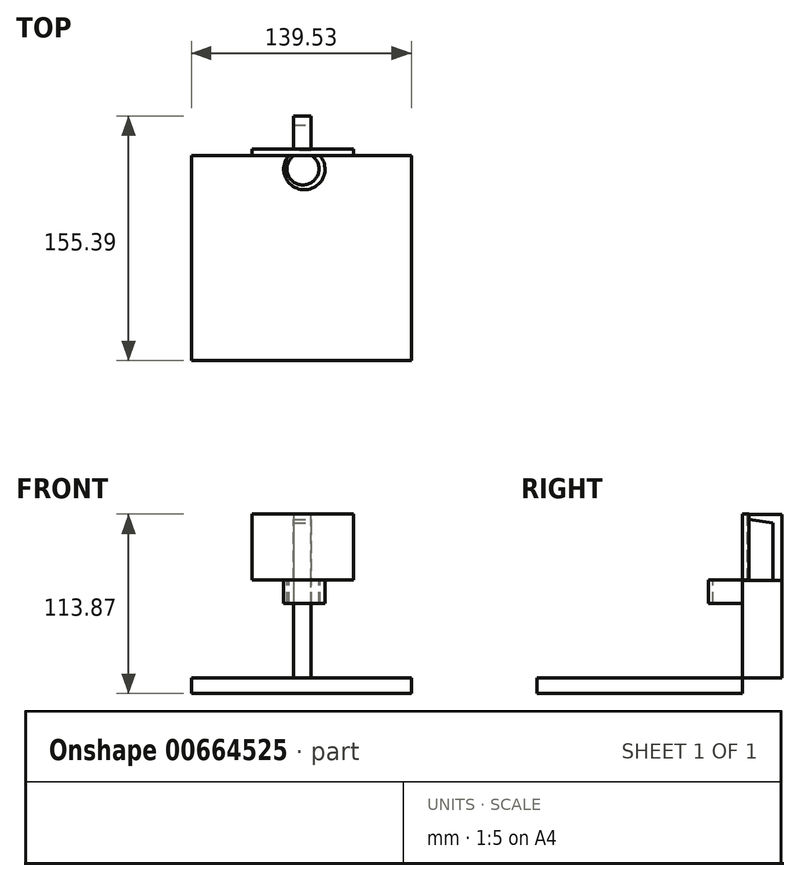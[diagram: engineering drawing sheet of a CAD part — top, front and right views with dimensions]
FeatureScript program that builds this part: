
annotation { "Feature Type Name" : "Feature", "Feature Type Description" : "" }
export const myFeature = defineFeature(function(context is Context, id is Id, definition is map)
    precondition{}
    {
        {
            var Q0;
            Q0=qCreatedBy(makeId("Top.planeOp"),FACE);
            var sketch = newSketch(context, id + "F0", { "sketchPlane" : qUnion([Q0])});
            skLineSegment(sketch, "E0", {"start": v(-70.05, 65.48) * mm, "end": v(-70.05, -64.91) * mm});
            skLineSegment(sketch, "E1", {"start": v(-70.05, -64.91) * mm, "end": v(69.48, -64.91) * mm});
            skLineSegment(sketch, "E2", {"start": v(69.48, -64.91) * mm, "end": v(69.48, 65.48) * mm});
            skLineSegment(sketch, "E3", {"start": v(69.48, 65.48) * mm, "end": v(-70.05, 65.48) * mm});
            skSolve(sketch);
        }
        {
            var Q0;
            Q0=makeQuery(id+"F0.imprint","IMPRINT",FACE,{"disambiguationData":[TD([[makeQuery(id+"F0.imprint","IMPRINT",EDGE,{"derivedFrom":sQuery(id+"F0.wireOp",EDGE,"E0")}),1.0]])]});
            extrude(context, id + "F1", {"entities" : qUnion([Q0]), "oppositeDirection" : true, "depth" : 10 * mm, "offsetDistance" : 25 * mm});
        }
        {
            var Q0;
            Q0=makeQuery(id+"F1.opExtrude","SWEPT_FACE",FACE,{"disambiguationData":[OSD([sQuery(id+"F0.wireOp",EDGE,"E3")])]});
            var sketch = newSketch(context, id + "F2", { "sketchPlane" : qUnion([Q0])});
            skLineSegment(sketch, "E4", {"start": v(-6.13, 0) * mm, "end": v(-6.13, 62.06) * mm});
            skLineSegment(sketch, "E5", {"start": v(-6.13, 62.06) * mm, "end": v(5.28, 62.06) * mm});
            skLineSegment(sketch, "E6", {"start": v(5.28, 62.06) * mm, "end": v(5.28, 0) * mm});
            skLineSegment(sketch, "E7", {"start": v(5.28, 0) * mm, "end": v(-6.13, 0) * mm});
            skLineSegment(sketch, "E8", {"start": v(-6.13, 62.06) * mm, "end": v(-32.65, 62.06) * mm});
            skLineSegment(sketch, "E9", {"start": v(-32.65, 62.06) * mm, "end": v(-32.65, 103.87) * mm});
            skLineSegment(sketch, "E10", {"start": v(-32.65, 103.87) * mm, "end": v(31.8, 103.87) * mm});
            skLineSegment(sketch, "E11", {"start": v(31.8, 103.87) * mm, "end": v(31.8, 62.06) * mm});
            skLineSegment(sketch, "E12", {"start": v(31.8, 62.06) * mm, "end": v(5.28, 62.06) * mm});
            skSolve(sketch);
        }
        {
            var Q0;
            Q0=makeQuery(id+"F2.imprint","IMPRINT",FACE,{"disambiguationData":[TD([[makeQuery(id+"F2.imprint","IMPRINT",EDGE,{"derivedFrom":sQuery(id+"F2.wireOp",EDGE,"E5")}),1.0]])]});
            extrude(context, id + "F3", {"entities" : qUnion([Q0]), "depth" : 4 * mm, "offsetDistance" : 25 * mm});
        }
        {
            var Q0;
            Q0=makeQuery(id+"F1.opExtrude","SWEPT_FACE",FACE,{"disambiguationData":[OSD([sQuery(id+"F0.wireOp",EDGE,"E3")])]});
            var sketch = newSketch(context, id + "F4", { "sketchPlane" : qUnion([Q0])});
            skLineSegment(sketch, "E13", {"start": v(5.27, 61.9) * mm, "end": v(5.27, 0) * mm});
            skLineSegment(sketch, "E14", {"start": v(5.27, 0) * mm, "end": v(-5.95, 0) * mm});
            skLineSegment(sketch, "E15", {"start": v(-5.95, 0) * mm, "end": v(-5.95, 61.9) * mm});
            skLineSegment(sketch, "E16", {"start": v(-5.95, 61.9) * mm, "end": v(5.27, 61.9) * mm});
            skSolve(sketch);
        }
        {
            var Q0;
            Q0=makeQuery(id+"F4.imprint","IMPRINT",FACE,{"disambiguationData":[TD([[makeQuery(id+"F4.imprint","IMPRINT",EDGE,{"derivedFrom":sQuery(id+"F4.wireOp",EDGE,"E13")}),-1.0]])]});
            extrude(context, id + "F5", {"entities" : qUnion([Q0]), "depth" : 25 * mm, "offsetDistance" : 25 * mm});
        }
        {
            var Q0;
            Q0=makeQuery(id+"F5.opExtrude","CAP_FACE",FACE,{"disambiguationData":[OSD([sQuery(id+"F4.wireOp",EDGE,"E13"),sQuery(id+"F4.wireOp",EDGE,"E14"),sQuery(id+"F4.wireOp",EDGE,"E15"),sQuery(id+"F4.wireOp",EDGE,"E16")])],"isStart":false});
            var sketch = newSketch(context, id + "F6", { "sketchPlane" : qUnion([Q0])});
            skLineSegment(sketch, "E17", {"start": v(-5.95, 61.9) * mm, "end": v(-5.95, 103.76) * mm});
            skLineSegment(sketch, "E18", {"start": v(-5.95, 103.76) * mm, "end": v(5.27, 103.76) * mm});
            skLineSegment(sketch, "E19", {"start": v(5.27, 103.76) * mm, "end": v(5.27, 61.9) * mm});
            skLineSegment(sketch, "E20", {"start": v(5.27, 61.9) * mm, "end": v(-5.95, 61.9) * mm});
            skSolve(sketch);
        }
        {
            var Q0;
            Q0 = qSketchRegion(id + "F6", true);
            extrude(context, id + "F7", {"entities" : qUnion([Q0]), "oppositeDirection" : true, "depth" : 22 * mm, "offsetDistance" : 25 * mm});
        }
        {
            var Q0;
            Q0=makeQuery(id+"F7.opExtrude","SWEPT_FACE",FACE,{"disambiguationData":[OSD([sQuery(id+"F6.wireOp",EDGE,"E17")])]});
            var sketch = newSketch(context, id + "F8", { "sketchPlane" : qUnion([Q0])});
            skLineSegment(sketch, "E21", {"start": v(84.8, 98.3) * mm, "end": v(84.8, 61.9) * mm});
            skLineSegment(sketch, "E22", {"start": v(84.8, 61.9) * mm, "end": v(69.5, 61.9) * mm});
            skLineSegment(sketch, "E23", {"start": v(69.5, 61.9) * mm, "end": v(69.5, 100.44) * mm});
            skLineSegment(sketch, "E24", {"start": v(69.5, 100.44) * mm, "end": v(84.8, 98.3) * mm});
            skSolve(sketch);
        }
        {
            var Q0;
            Q0=makeQuery(id+"F8.imprint","IMPRINT",FACE,{"disambiguationData":[TD([[makeQuery(id+"F8.imprint","IMPRINT",EDGE,{"derivedFrom":sQuery(id+"F8.wireOp",EDGE,"E21")}),-1.0]])]});
            extrude(context, id + "F9", {"entities" : qUnion([Q0]), "operationType" : NewBodyOperationType.REMOVE, "oppositeDirection" : true, "depth" : 25 * mm, "offsetDistance" : 25 * mm});
        }
        {
            var Q0;
            Q0=makeQuery(id+"F3.opExtrude","SWEPT_FACE",FACE,{"disambiguationData":[OSD([sQuery(id+"F2.wireOp",EDGE,"E5"),sQuery(id+"F2.wireOp",EDGE,"E8"),sQuery(id+"F2.wireOp",EDGE,"E12")])]});
            var sketch = newSketch(context, id + "F10", { "sketchPlane" : qUnion([Q0])});
            skPoint(sketch, "E25.first.point", {"position": v(0, -65.48) * mm});
            skArc(sketch, "E26", {"start": v(11.4, -65.48) * mm, "mid": v(1.6, -43.7) * mm, "end": v(-8.2, -65.48) * mm});
            skSolve(sketch);
        }
        {
            var Q0;
            {var subQ0=sQuery(id+"F10.wireOp",EDGE,"E26");Q0=makeQuery(id+"F10.imprint","IMPRINT",FACE,{"disambiguationData":[TD([[makeQuery(id+"F10.imprint","IMPRINT",EDGE,{"derivedFrom":subQ0}),1.0]])]});}
            extrude(context, id + "F11", {"entities" : qUnion([Q0]), "operationType" : NewBodyOperationType.ADD, "depth" : 15 * mm, "offsetDistance" : 25 * mm});
        }
        {
            var Q0;
            Q0=makeQuery(id+"F11.opExtrude","CAP_FACE",FACE,{"disambiguationData":[OSD([sQuery(id+"F2.wireOp",EDGE,"E5"),sQuery(id+"F2.wireOp",EDGE,"E8"),sQuery(id+"F2.wireOp",EDGE,"E12"),sQuery(id+"F10.wireOp",EDGE,"E26")])],"isStart":true});
            var sketch = newSketch(context, id + "F12", { "sketchPlane" : qUnion([Q0])});
            skArc(sketch, "E27", {"start": v(-4.88, 65.48) * mm, "mid": v(0.63, 46.69) * mm, "end": v(6.14, 65.48) * mm});
            skSolve(sketch);
        }
        {
            var Q0;
            {var subQ0=sQuery(id+"F12.wireOp",EDGE,"E27");Q0=makeQuery(id+"F12.imprint","IMPRINT",FACE,{"disambiguationData":[TD([[makeQuery(id+"F12.imprint","IMPRINT",EDGE,{"derivedFrom":subQ0}),1.0]])]});}
            extrude(context, id + "F13", {"entities" : qUnion([Q0]), "operationType" : NewBodyOperationType.REMOVE, "oppositeDirection" : true, "depth" : 25 * mm, "offsetDistance" : 25 * mm});
        }
    });
